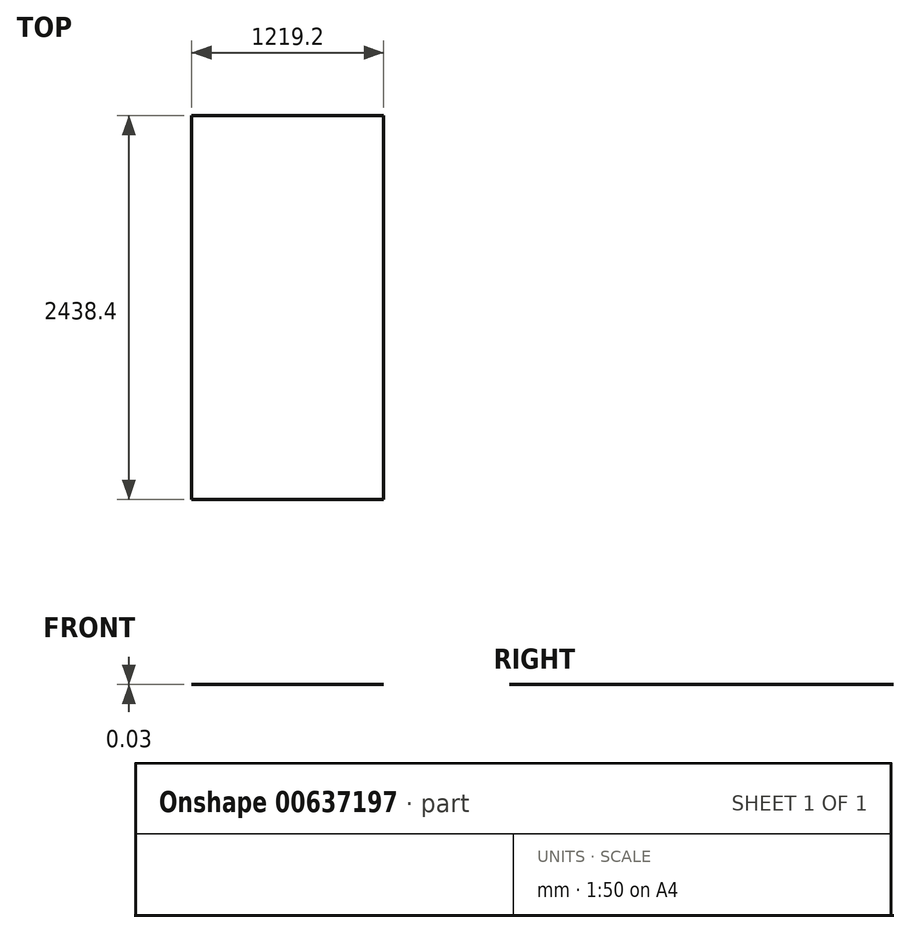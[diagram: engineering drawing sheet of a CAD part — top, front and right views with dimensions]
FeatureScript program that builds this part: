
annotation { "Feature Type Name" : "Feature", "Feature Type Description" : "" }
export const myFeature = defineFeature(function(context is Context, id is Id, definition is map)
    precondition{}
    {
        {
            var Q0;
            Q0=qCreatedBy(makeId("Top.planeOp"),FACE);
            var sketch = newSketch(context, id + "F0", { "sketchPlane" : qUnion([Q0])});
            skLineSegment(sketch, "E0.bottom", {"start": v(-608.05, 1581.3) * mm, "end": v(611.15, 1581.3) * mm});
            skLineSegment(sketch, "E0.top", {"start": v(-608.05, -857.1) * mm, "end": v(611.15, -857.1) * mm});
            skLineSegment(sketch, "E0.left", {"start": v(-608.05, 1581.3) * mm, "end": v(-608.05, -857.1) * mm});
            skLineSegment(sketch, "E0.right", {"start": v(611.15, 1581.3) * mm, "end": v(611.15, -857.1) * mm});
            skSolve(sketch);
        }
        {
            var Q0;
            Q0=makeQuery(id+"F0.imprint","IMPRINT",FACE,{"disambiguationData":[TD([[makeQuery(id+"F0.imprint","IMPRINT",EDGE,{"derivedFrom":sQuery(id+"F0.wireOp",EDGE,"E0.bottom")}),-1.0]])]});
            extrude(context, id + "F1", {"entities" : qUnion([Q0]), "depth" : 3 / 101.6 * mm, "offsetDistance" : 25.4 * mm});
        }
    });
